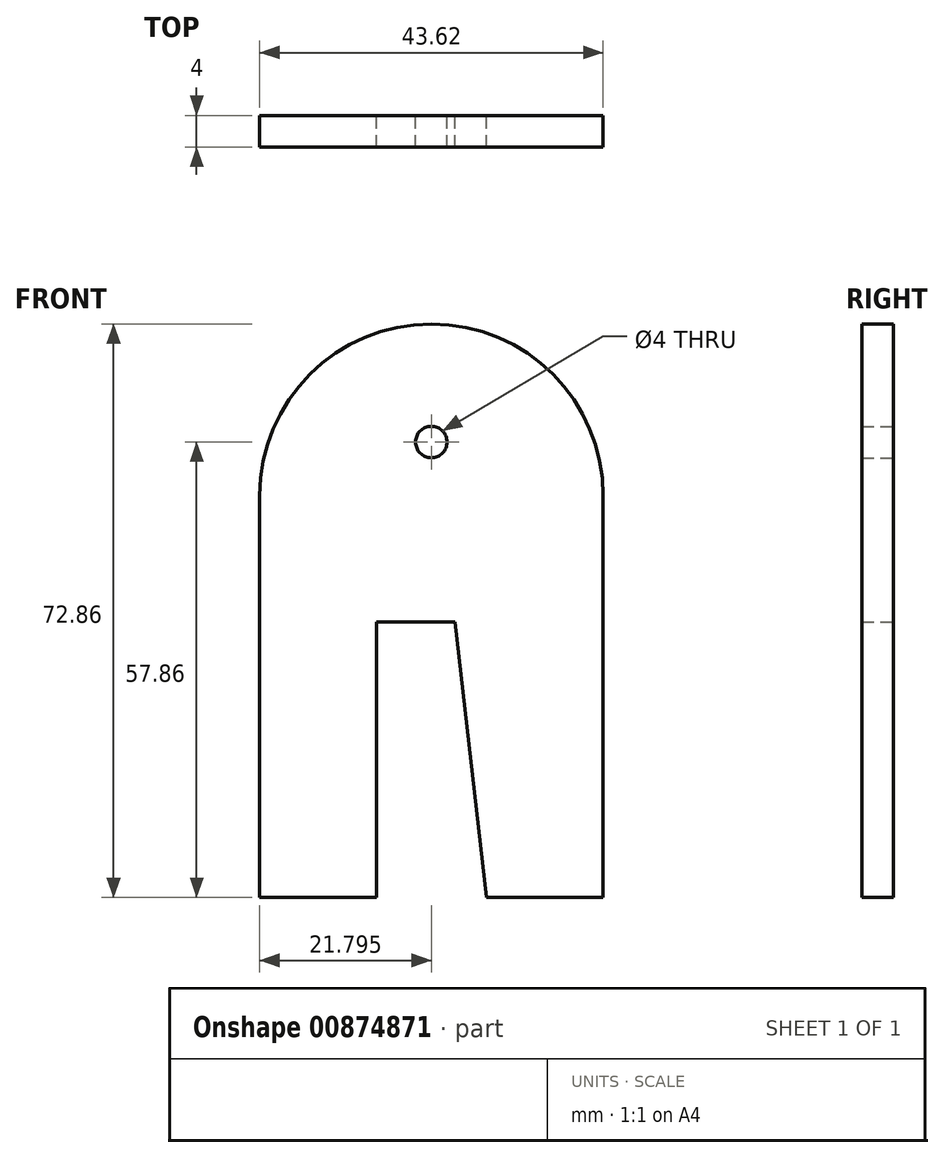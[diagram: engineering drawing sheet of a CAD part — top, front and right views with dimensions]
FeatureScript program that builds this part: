
annotation { "Feature Type Name" : "Feature", "Feature Type Description" : "" }
export const myFeature = defineFeature(function(context is Context, id is Id, definition is map)
    precondition{}
    {
        {
            var Q0;
            Q0=qCreatedBy(makeId("Front.planeOp"),FACE);
            var sketch = newSketch(context, id + "F0", { "sketchPlane" : qUnion([Q0])});
            skLineSegment(sketch, "E0", {"start": v(140.8, -242.23) * mm, "end": v(136.8, -207.23) * mm});
            skLineSegment(sketch, "E1", {"start": v(136.8, -207.23) * mm, "end": v(126.8, -207.23) * mm});
            skLineSegment(sketch, "E2", {"start": v(126.8, -207.23) * mm, "end": v(126.8, -242.23) * mm});
            skLineSegment(sketch, "E3", {"start": v(126.8, -242.23) * mm, "end": v(111.98, -242.23) * mm});
            skLineSegment(sketch, "E4", {"start": v(111.98, -242.23) * mm, "end": v(111.98, -191.18) * mm});
            skLineSegment(sketch, "E5", {"start": v(140.8, -242.23) * mm, "end": v(155.6, -242.23) * mm});
            skLineSegment(sketch, "E6", {"start": v(155.6, -242.23) * mm, "end": v(155.6, -191.18) * mm});
            skArc(sketch, "E7", {"start": v(155.6, -191.18) * mm, "mid": v(133.8, -169.37) * mm, "end": v(111.98, -191.18) * mm});
            skCircle(sketch, "E8", {"center": v(133.78, -184.37) * mm, "radius": 2 * mm});
            skLineSegment(sketch, "E9", {"start": v(126.8, -242.23) * mm, "end": v(207.8, -242.23) * mm, "construction": true});
            skSolve(sketch);
        }
        {
            var Q0;
            Q0=makeQuery(id+"F0.imprint","IMPRINT",FACE,{"disambiguationData":[TD([[makeQuery(id+"F0.imprint","IMPRINT",EDGE,{"derivedFrom":sQuery(id+"F0.wireOp",EDGE,"E0")}),-1.0]])]});
            extrude(context, id + "F1", {"entities" : qUnion([Q0]), "depth" : 4 * mm, "offsetDistance" : 25 * mm});
        }
    });
